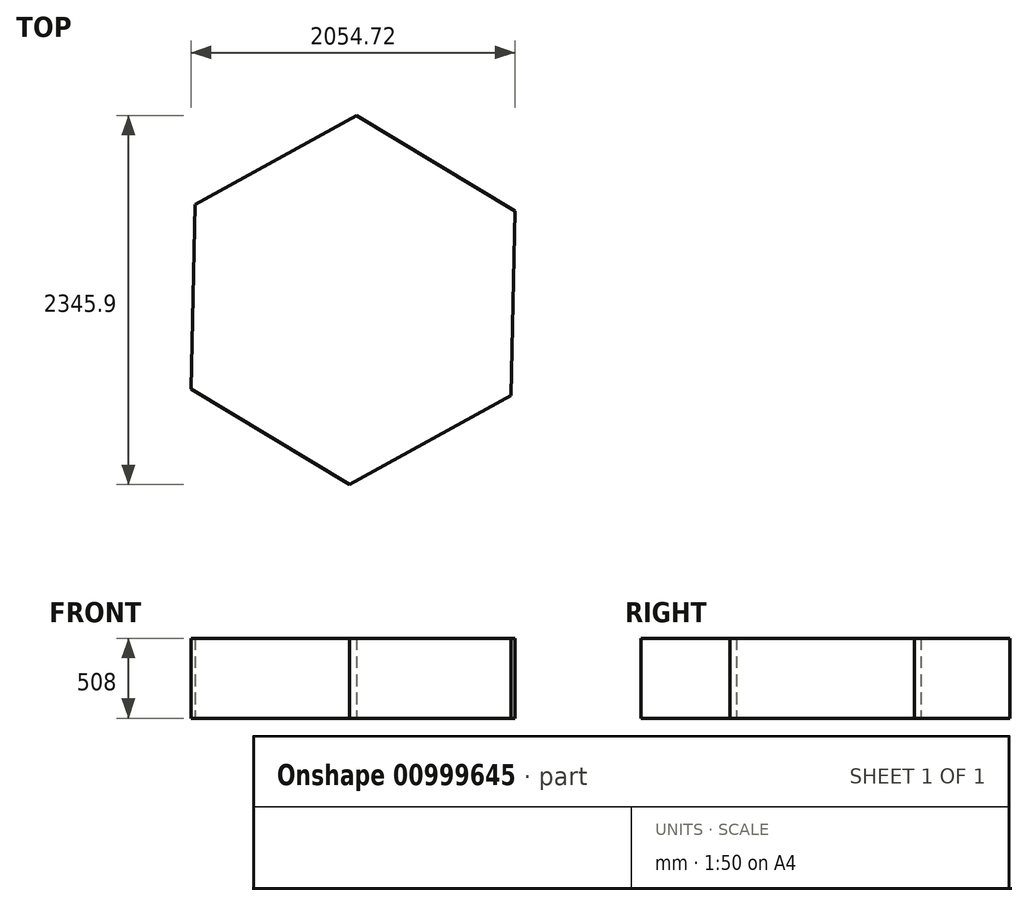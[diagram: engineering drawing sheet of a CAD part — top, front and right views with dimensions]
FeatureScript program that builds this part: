
annotation { "Feature Type Name" : "Feature", "Feature Type Description" : "" }
export const myFeature = defineFeature(function(context is Context, id is Id, definition is map)
    precondition{}
    {
        {
            var Q0;
            Q0=qCreatedBy(makeId("Top.planeOp"),FACE);
            var sketch = newSketch(context, id + "F0", { "sketchPlane" : qUnion([Q0])});
            skCircle(sketch, "E0.cCircle", {"center": v(0, 108.94) * mm, "radius": 1016 * mm, "construction": true});
            skLineSegment(sketch, "E0.0", {"start": v(-1004.24, 715.44) * mm, "end": v(23.12, 1281.89) * mm});
            skLineSegment(sketch, "E0.1", {"start": v(23.12, 1281.89) * mm, "end": v(1027.36, 675.4) * mm});
            skLineSegment(sketch, "E0.2", {"start": v(1027.36, 675.4) * mm, "end": v(1004.24, -497.55) * mm});
            skLineSegment(sketch, "E0.3", {"start": v(1004.24, -497.55) * mm, "end": v(-23.12, -1064) * mm});
            skLineSegment(sketch, "E0.4", {"start": v(-23.12, -1064) * mm, "end": v(-1027.36, -457.51) * mm});
            skLineSegment(sketch, "E0.5", {"start": v(-1027.36, -457.51) * mm, "end": v(-1004.24, 715.44) * mm});
            skPoint(sketch, "E0.0.midPoint", {"position": v(-490.56, 998.66) * mm});
            skSolve(sketch);
        }
        {
            var Q0;
            Q0 = qSketchRegion(id + "F0", true);
            extrude(context, id + "F1", {"entities" : qUnion([Q0]), "depth" : 508 * mm, "offsetDistance" : 25.4 * mm});
        }
    });
